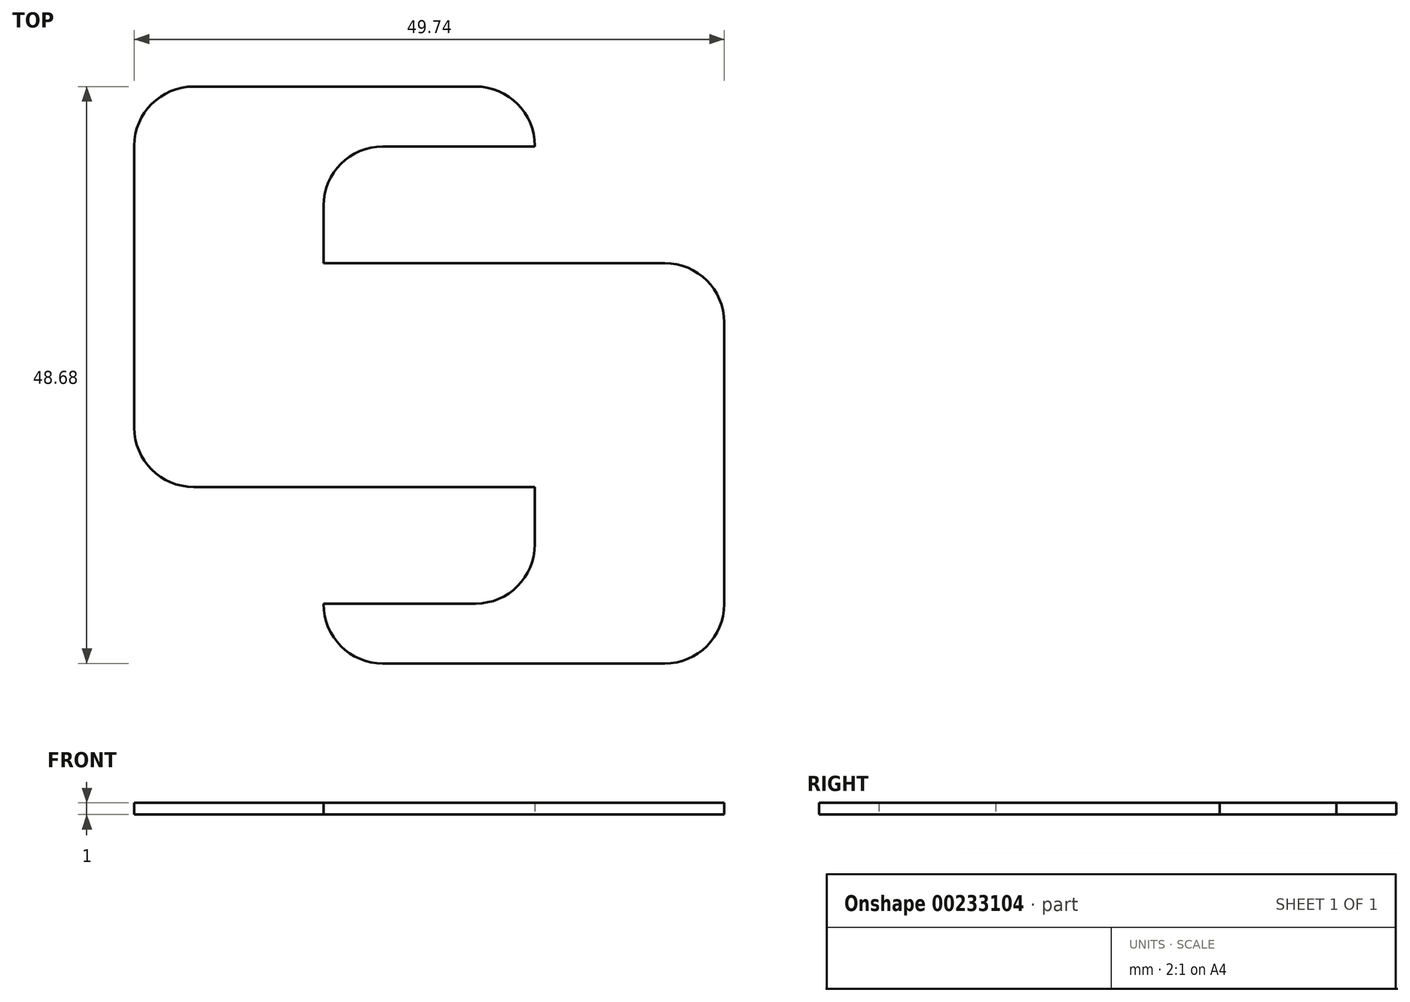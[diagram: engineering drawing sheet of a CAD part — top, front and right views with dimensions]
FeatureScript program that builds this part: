
annotation { "Feature Type Name" : "Feature", "Feature Type Description" : "" }
export const myFeature = defineFeature(function(context is Context, id is Id, definition is map)
    precondition{}
    {
        {
            var Q0;
            Q0=qCreatedBy(makeId("Top.planeOp"),FACE);
            var sketch = newSketch(context, id + "F0", { "sketchPlane" : qUnion([Q0])});
            skLineSegment(sketch, "E0", {"start": v(-3.2, 48.68) * mm, "end": v(-26.98, 48.68) * mm});
            skLineSegment(sketch, "E1", {"start": v(-31.98, 43.68) * mm, "end": v(-31.98, 19.9) * mm});
            skLineSegment(sketch, "E2", {"start": v(-26.98, 14.9) * mm, "end": v(1.8, 14.9) * mm});
            skLineSegment(sketch, "E3", {"start": v(1.8, 14.9) * mm, "end": v(1.8, 10.05) * mm});
            skLineSegment(sketch, "E4", {"start": v(-3.2, 5.05) * mm, "end": v(-16.02, 5.05) * mm});
            skLineSegment(sketch, "E5", {"start": v(-16.02, 5.05) * mm, "end": v(-16.02, 5) * mm});
            skLineSegment(sketch, "E6", {"start": v(-11.02, 0) * mm, "end": v(12.76, 0) * mm});
            skLineSegment(sketch, "E7", {"start": v(17.76, 5) * mm, "end": v(17.76, 28.78) * mm});
            skLineSegment(sketch, "E8", {"start": v(12.76, 33.78) * mm, "end": v(-16.02, 33.78) * mm});
            skLineSegment(sketch, "E9", {"start": v(-16.02, 33.78) * mm, "end": v(-16.02, 38.62) * mm});
            skLineSegment(sketch, "E10", {"start": v(-11.02, 43.62) * mm, "end": v(1.8, 43.62) * mm});
            skLineSegment(sketch, "E11", {"start": v(1.8, 43.62) * mm, "end": v(1.8, 43.68) * mm});
            skPoint(sketch, "E12.visualSharp", {"position": v(-31.98, 48.68) * mm});
            skArc(sketch, "E12.filletArc", {"start": v(-26.98, 48.68) * mm, "mid": v(-30.52, 47.21) * mm, "end": v(-31.98, 43.68) * mm});
            skPoint(sketch, "E13.visualSharp", {"position": v(-31.98, 14.9) * mm});
            skArc(sketch, "E13.filletArc", {"start": v(-31.98, 19.9) * mm, "mid": v(-30.52, 16.36) * mm, "end": v(-26.98, 14.9) * mm});
            skPoint(sketch, "E14.visualSharp", {"position": v(17.76, 33.78) * mm});
            skArc(sketch, "E14.filletArc", {"start": v(17.76, 28.78) * mm, "mid": v(16.3, 32.32) * mm, "end": v(12.76, 33.78) * mm});
            skPoint(sketch, "E15.visualSharp", {"position": v(17.76, 0) * mm});
            skArc(sketch, "E15.filletArc", {"start": v(12.76, 0) * mm, "mid": v(16.3, 1.46) * mm, "end": v(17.76, 5) * mm});
            skPoint(sketch, "E16.visualSharp", {"position": v(-16.02, 0) * mm});
            skArc(sketch, "E16.filletArc", {"start": v(-16.02, 5) * mm, "mid": v(-14.56, 1.46) * mm, "end": v(-11.02, 0) * mm});
            skPoint(sketch, "E17.visualSharp", {"position": v(1.8, 5.05) * mm});
            skArc(sketch, "E17.filletArc", {"start": v(-3.2, 5.05) * mm, "mid": v(0.33, 6.52) * mm, "end": v(1.8, 10.05) * mm});
            skPoint(sketch, "E18.visualSharp", {"position": v(1.8, 48.68) * mm});
            skArc(sketch, "E18.filletArc", {"start": v(1.8, 43.68) * mm, "mid": v(0.33, 47.21) * mm, "end": v(-3.2, 48.68) * mm});
            skPoint(sketch, "E19.visualSharp", {"position": v(-16.02, 43.62) * mm});
            skArc(sketch, "E19.filletArc", {"start": v(-11.02, 43.62) * mm, "mid": v(-14.56, 42.16) * mm, "end": v(-16.02, 38.62) * mm});
            skSolve(sketch);
        }
        {
            var Q0;
            Q0=makeQuery(id+"F0.imprint","IMPRINT",FACE,{"disambiguationData":[TD([[makeQuery(id+"F0.imprint","IMPRINT",EDGE,{"derivedFrom":sQuery(id+"F0.wireOp",EDGE,"E0")}),1.0]])]});
            extrude(context, id + "F1", {"entities" : qUnion([Q0]), "depth" : 1 * mm});
        }
    });
